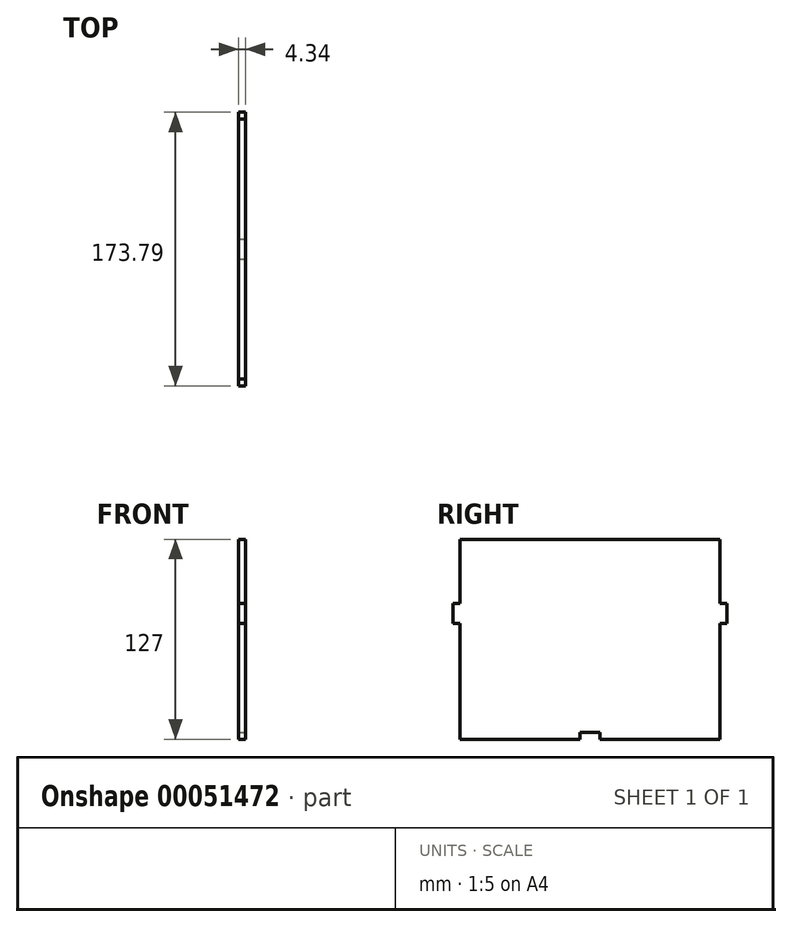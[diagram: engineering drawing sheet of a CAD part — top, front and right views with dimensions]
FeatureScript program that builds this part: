
annotation { "Feature Type Name" : "Feature", "Feature Type Description" : "" }
export const myFeature = defineFeature(function(context is Context, id is Id, definition is map)
    precondition{}
    {
        {
            var Q0;
            Q0=qCreatedBy(makeId("Right.planeOp"),FACE);
            var sketch = newSketch(context, id + "F0", { "sketchPlane" : qUnion([Q0])});
            skLineSegment(sketch, "E0.bottom", {"start": v(-53.18, 79.9) * mm, "end": v(111.92, 79.9) * mm});
            skLineSegment(sketch, "E0.top", {"start": v(-53.18, -47.1) * mm, "end": v(111.92, -47.1) * mm});
            skLineSegment(sketch, "E0.left", {"start": v(-53.18, 79.9) * mm, "end": v(-53.18, -47.1) * mm});
            skLineSegment(sketch, "E0.right", {"start": v(111.92, 79.9) * mm, "end": v(111.92, -47.1) * mm});
            skLineSegment(sketch, "E1.bottom", {"start": v(-53.18, 39.27) * mm, "end": v(-57.52, 39.27) * mm});
            skLineSegment(sketch, "E1.top", {"start": v(-53.18, 26.57) * mm, "end": v(-57.52, 26.57) * mm});
            skLineSegment(sketch, "E1.left", {"start": v(-53.18, 39.27) * mm, "end": v(-53.18, 26.57) * mm});
            skLineSegment(sketch, "E1.right", {"start": v(-57.52, 39.27) * mm, "end": v(-57.52, 26.57) * mm});
            skLineSegment(sketch, "E2.0", {"start": v(-53.18, 39.25) * mm, "end": v(111.92, 39.25) * mm, "construction": true});
            skLineSegment(sketch, "E3.0", {"start": v(23.02, 79.9) * mm, "end": v(23.02, -47.1) * mm, "construction": true});
            skLineSegment(sketch, "E4.0", {"start": v(35.72, 79.9) * mm, "end": v(35.72, -47.1) * mm, "construction": true});
            skLineSegment(sketch, "E5.bottom", {"start": v(23.02, -47.1) * mm, "end": v(35.72, -47.1) * mm});
            skLineSegment(sketch, "E5.top", {"start": v(23.02, -42.76) * mm, "end": v(35.72, -42.76) * mm});
            skLineSegment(sketch, "E5.left", {"start": v(23.02, -47.1) * mm, "end": v(23.02, -42.76) * mm});
            skLineSegment(sketch, "E5.right", {"start": v(35.72, -47.1) * mm, "end": v(35.72, -42.76) * mm});
            skLineSegment(sketch, "E6.0", {"start": v(29.37, 79.9) * mm, "end": v(29.37, -47.1) * mm, "construction": true});
            skLineSegment(sketch, "E7.MirrorCS", {"start": v(116.27, 39.27) * mm, "end": v(116.27, 26.57) * mm});
            skLineSegment(sketch, "E8.MirrorCS", {"start": v(111.92, 39.27) * mm, "end": v(116.27, 39.27) * mm});
            skLineSegment(sketch, "E9.MirrorCS", {"start": v(111.92, 26.57) * mm, "end": v(116.27, 26.57) * mm});
            skLineSegment(sketch, "E10.MirrorCS", {"start": v(111.92, 39.27) * mm, "end": v(111.92, 26.57) * mm});
            skSolve(sketch);
        }
        {
            var Q0;
            Q0=qSketchRegion(id+"F0",true);
            extrude(context, id + "F1", {"entities" : qUnion([Q0]), "oppositeDirection" : true, "depth" : 4.34 * mm});
        }
        {
            var Q0;
            Q0=qCreatedBy(makeId("Right.planeOp"),FACE);
            var sketch = newSketch(context, id + "F2", { "sketchPlane" : qUnion([Q0])});
            skLineSegment(sketch, "E11.0", {"start": v(23.02, 26.57) * mm, "end": v(23.02, -47.1) * mm, "construction": true});
            skLineSegment(sketch, "E12.0", {"start": v(35.72, 79.9) * mm, "end": v(35.72, -47.1) * mm, "construction": true});
            skLineSegment(sketch, "E13.0", {"start": v(23.02, 79.9) * mm, "end": v(23.02, 39.27) * mm, "construction": true});
            skLineSegment(sketch, "E14.0", {"start": v(23.02, 39.27) * mm, "end": v(23.02, 26.57) * mm, "construction": true});
            skLineSegment(sketch, "E15.bottom", {"start": v(23.02, -42.76) * mm, "end": v(35.72, -42.76) * mm});
            skLineSegment(sketch, "E15.top", {"start": v(23.02, -47.1) * mm, "end": v(35.72, -47.1) * mm});
            skLineSegment(sketch, "E15.left", {"start": v(23.02, -42.76) * mm, "end": v(23.02, -47.1) * mm});
            skLineSegment(sketch, "E15.right", {"start": v(35.72, -42.76) * mm, "end": v(35.72, -47.1) * mm});
            skSolve(sketch);
        }
        {
            var Q0;
            Q0=qSketchRegion(id+"F2",true);
            extrude(context, id + "F3", {"entities" : qUnion([Q0]), "operationType" : NewBodyOperationType.REMOVE, "endBound" : BoundingType.THROUGH_ALL, "oppositeDirection" : true, "depth" : 25.4 * mm});
        }
    });
